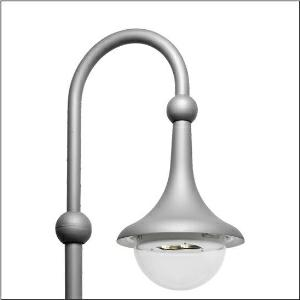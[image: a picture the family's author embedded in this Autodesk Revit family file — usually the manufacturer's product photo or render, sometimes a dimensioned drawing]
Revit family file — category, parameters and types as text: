
# Revit family: grosse_glocke___st1_2a_5xa1563k1b108_1a11
name_source: partatom
category: Lighting Fixtures
units: mm (PartAtom-declared; Revit-internal decimal feet)

## family parameters
Cut with Voids When Loaded = No
Host = Face
Light Source = No
Part Type = Normal
Room Calculation Point = No
Round Connector Dimension = Use Diameter
Shared = No

## types (1)
- --- (1 x LED, 3320 lm, 23.4 W, 4000K)
    Apparent Load = 23 VA
    CIE Flux Codes = 29 66 95 99 100
    Color Rendering = 70
    Color Temperature = 4000K
    Default Elevation = 1800 mm
    Description = Large Bell, mast luminaire, primary light control with 3 zone facetted reflector, of plastic, silver coated, primary optical cover: enclosure, of PMMA, transparent, light distribution: ST1.2a, light emission: direct distribution, primary light characteristic: asymmetric, installation type: suspended mounting, LED, High Power LED, rated luminous flux: 3.320lm, luminous efficacy: 142lm/W, light colour: 740, colour temperature: 4000K, control gear: ECG Plus, control: flexible luminous flux parameterisation, time-dependent luminous flux control, constant luminous flux control, digital communication interface, power reduction, electronic power reduction, mains connection: 230..240V, AC, 50/60Hz, start of lifetime: 23W, end of service life: 24W, reduction: 12W, luminaire housing, bell-shaped, of glass-fibre reinforced polyester, coated, Siteco® metallic grey (DB 702S), please order curved mast extension separately, diameter: 530mm, height: 695mm, protection rating (complete): IP54, insulation class (complete): insulation class II (safety insulation), certification: CE, ENEC, VDE, impact resistance: IK08, standard-compliant lighting for roads and squares, packaging unit: 1 piece

Light Distribution: ST1.2a
    Height = 695 mm
    Lamp = 1 x LED
    Lamp Light Flux = 3320 lm
    Lamp Power = 23.4 W
    Lamp count = 1
    Length = 530 mm
    Luminous efficacy = 142 lm/W
    Manufacturer = Siteco
    ModVariant = No
    Model = 5XA1563K1B108
    Number of Poles = 1
    OnlyDefault = Yes
    Power Factor = 1
    Product Name = Große Glocke | ST1.2a
    Product group = mast luminaire | pylon annexe
    ProductGroupID = 6201
    Protection Class = Protection class II
    Protection Degree = IP 54
    RLX_Detail_Level = 1
    RLX_Emergency_Light_Flux = 0 lm
    RLX_Emergency_Type = 0
    RLX_Emergency_Type_DB = No
    RlxData = <blob elided: 52793 chars, md5=581adcf0>
    Socket = socket
    Standby Power = 0 W
    System Light Flux = 3320 lm
    System Power = 23 W
    Type Comments = factory setting: luminous flux: 100 % | dim-lin: 254 | 460 mA
    Type Image = l_1284381.jpg
    URL = http://relux.com
    VarID = @adj_137439
    Voltage = 0 V
    Weight = 0.00 kg
    Width = 0 mm  [stored 0 ft]

note: [stored X ft] marks values corroborated as IEEE doubles in the binary element streams (Revit-internal decimal feet)

## geometry (parser evidence)
native form markers: Blend x4, Sweep x12
no freeform markers — native parametric forms only
